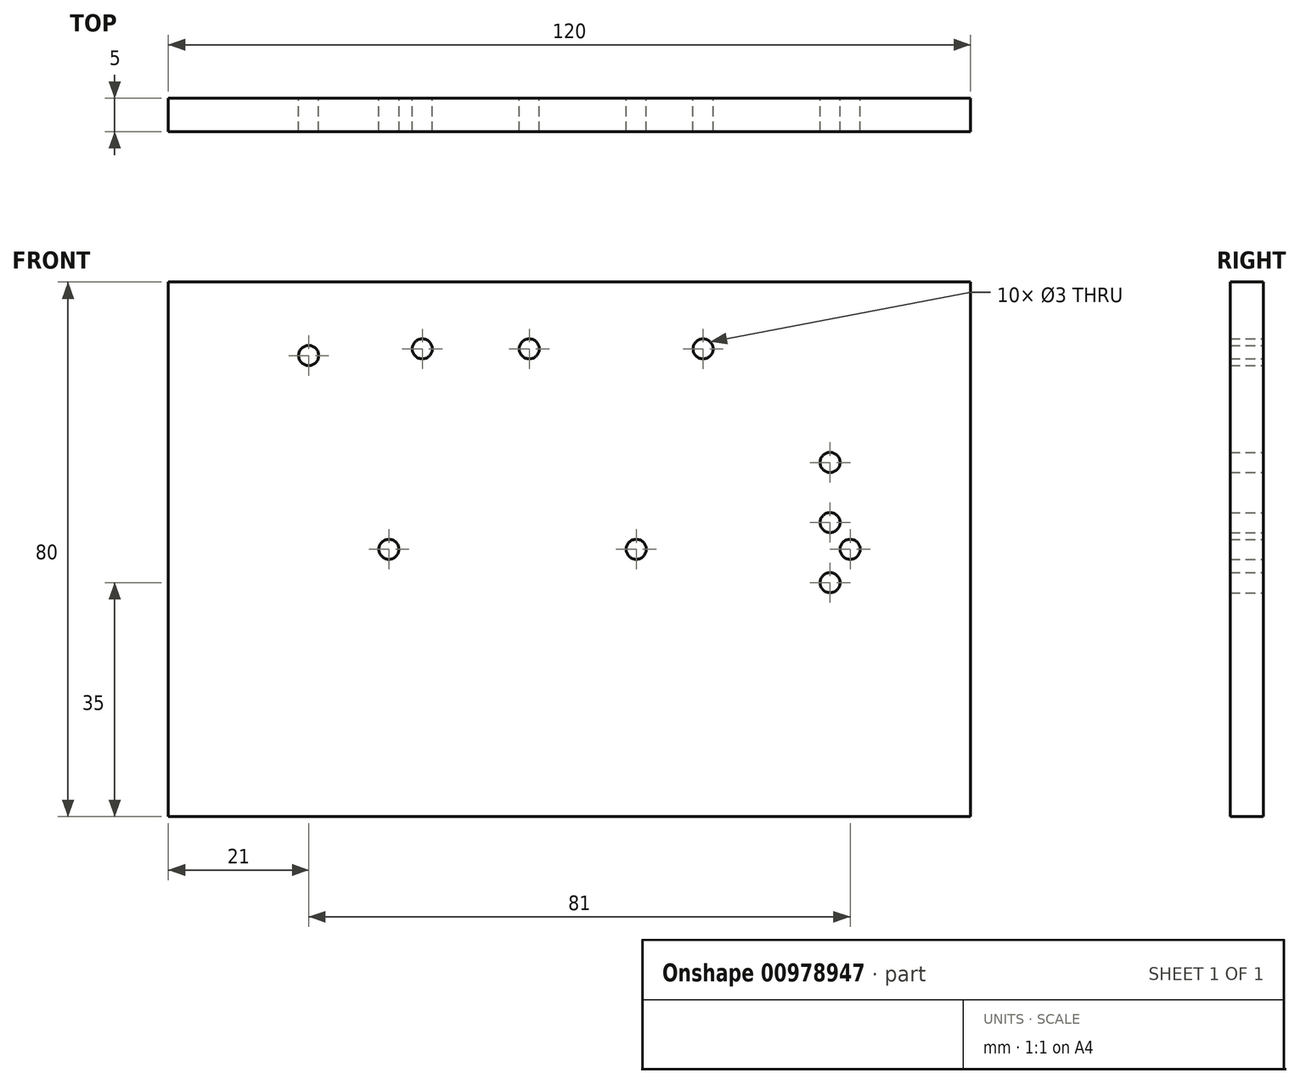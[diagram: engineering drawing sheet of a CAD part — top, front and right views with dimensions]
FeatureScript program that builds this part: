
annotation { "Feature Type Name" : "Feature", "Feature Type Description" : "" }
export const myFeature = defineFeature(function(context is Context, id is Id, definition is map)
    precondition{}
    {
        {
            var Q0;
            Q0=qCreatedBy(makeId("Front.planeOp"),FACE);
            var sketch = newSketch(context, id + "F0", { "sketchPlane" : qUnion([Q0])});
            skCircle(sketch, "E0", {"center": v(0, 0) * mm, "radius": 1.5 * mm});
            skCircle(sketch, "E1", {"center": v(29, 4) * mm, "radius": 1.5 * mm});
            skLineSegment(sketch, "E2.bottom", {"start": v(-70, 40) * mm, "end": v(50, 40) * mm});
            skLineSegment(sketch, "E2.top", {"start": v(-70, -40) * mm, "end": v(50, -40) * mm});
            skLineSegment(sketch, "E2.left", {"start": v(-70, 40) * mm, "end": v(-70, -40) * mm});
            skLineSegment(sketch, "E2.right", {"start": v(50, 40) * mm, "end": v(50, -40) * mm});
            skCircle(sketch, "E3", {"center": v(-37, 0) * mm, "radius": 1.5 * mm});
            skCircle(sketch, "E4", {"center": v(29, 13) * mm, "radius": 1.5 * mm});
            skCircle(sketch, "E5", {"center": v(29, -5) * mm, "radius": 1.5 * mm});
            skCircle(sketch, "E6", {"center": v(-49, 29) * mm, "radius": 1.5 * mm});
            skCircle(sketch, "E7", {"center": v(10, 30) * mm, "radius": 1.5 * mm});
            skCircle(sketch, "E8", {"center": v(-16, 30) * mm, "radius": 1.5 * mm});
            skCircle(sketch, "E9", {"center": v(-32, 30) * mm, "radius": 1.5 * mm});
            skCircle(sketch, "E10", {"center": v(32, 0) * mm, "radius": 1.5 * mm});
            skSolve(sketch);
        }
        {
            var Q0;
            Q0=makeQuery(id+"F0.imprint","IMPRINT",FACE,{"disambiguationData":[TD([[makeQuery(id+"F0.imprint","IMPRINT",EDGE,{"derivedFrom":sQuery(id+"F0.wireOp",EDGE,"E0")}),-1.0]])]});
            extrude(context, id + "F1", {"entities" : qUnion([Q0]), "depth" : 5 * mm, "offsetDistance" : 25 * mm});
        }
    });
